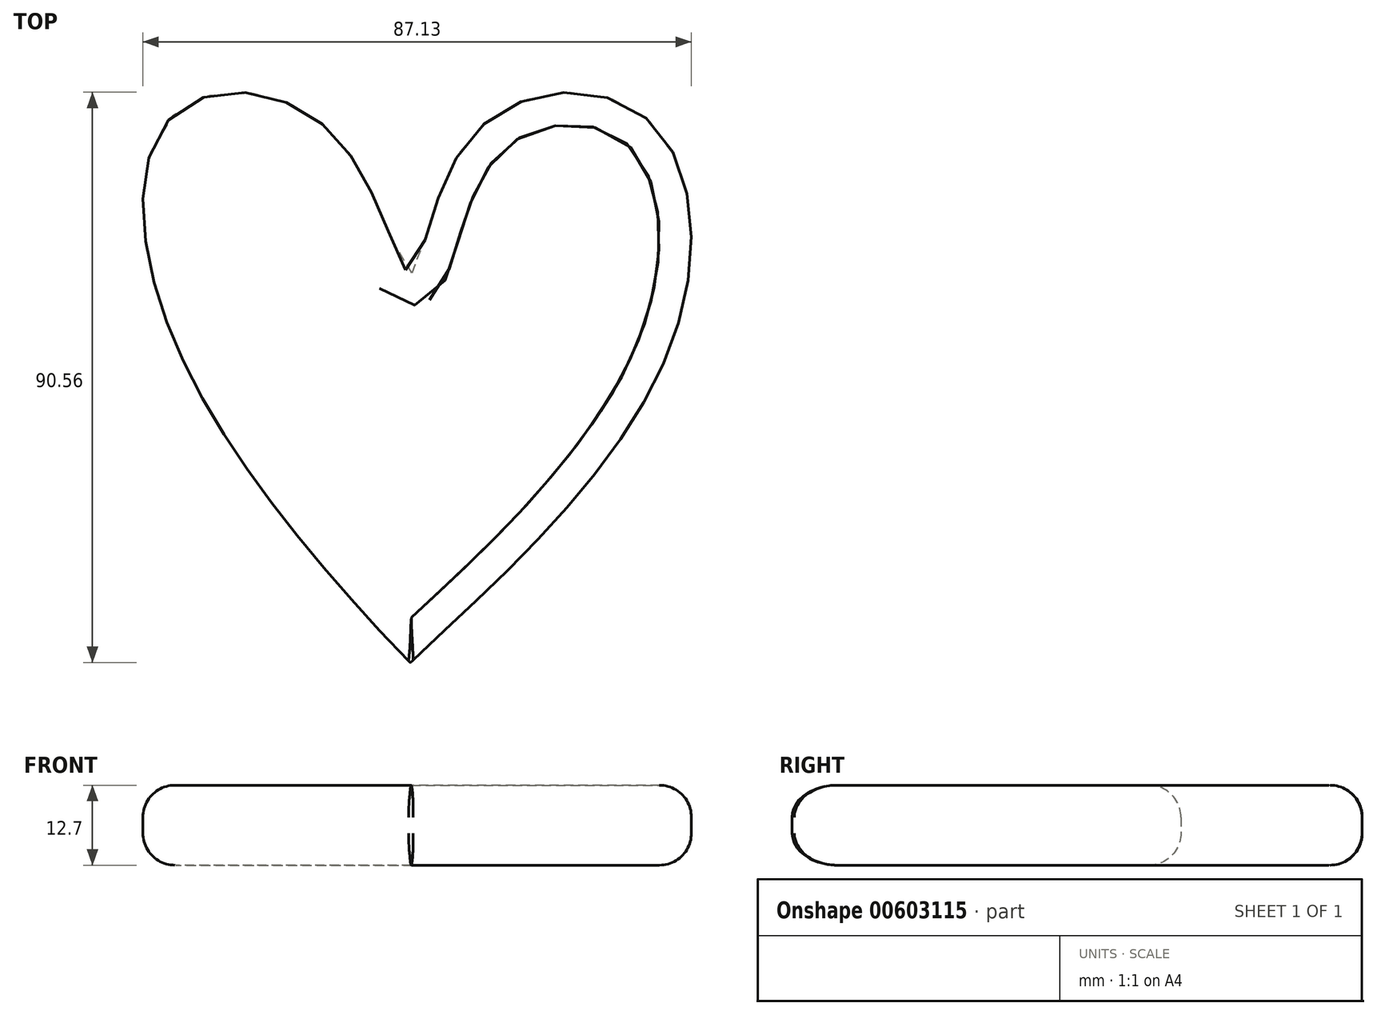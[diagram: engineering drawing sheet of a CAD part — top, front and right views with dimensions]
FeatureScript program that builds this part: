
annotation { "Feature Type Name" : "Feature", "Feature Type Description" : "" }
export const myFeature = defineFeature(function(context is Context, id is Id, definition is map)
    precondition{}
    {
        {
            var Q0;
            Q0=qCreatedBy(makeId("Top.planeOp"),FACE);
            var sketch = newSketch(context, id + "F0", { "sketchPlane" : qUnion([Q0])});
            skFitSpline(sketch, "E0", {"points": [v(0, 0) * mm, v(-0.14, 0.09) * mm, v(-34.43, 44.52) * mm, v(-37.1, 87.44) * mm, v(-11.8, 83.44) * mm, v(0, 61.76) * mm, v(9.57, 83.36) * mm, v(36.94, 86.87) * mm, v(40.09, 47.18) * mm, v(3.83, 3.6) * mm, v(0, 0) * mm]});
            skSolve(sketch);
        }
        {
            var Q0;
            Q0=makeQuery(id+"F0.imprint","IMPRINT",FACE,{"disambiguationData":[TD([[makeQuery(id+"F0.imprint","IMPRINT",EDGE,{"derivedFrom":sQuery(id+"F0.wireOp",EDGE,"E0")}),-1.0]])]});
            extrude(context, id + "F1", {"entities" : qUnion([Q0]), "oppositeDirection" : true, "depth" : 12.7 * mm, "offsetDistance" : 25.4 * mm});
        }
        {
            var Q0;
            Q0=makeQuery(id+"F1.opExtrude","CAP_EDGE",EDGE,{"disambiguationData":[OSD([sQuery(id+"F0.wireOp",EDGE,"E0"),sQuery(id+"F0.wireOp",EDGE,"E0")])],"isStart":true});
            var Q1;
            Q1=makeQuery(id+"F1.opExtrude","CAP_EDGE",EDGE,{"disambiguationData":[OSD([sQuery(id+"F0.wireOp",EDGE,"E0"),sQuery(id+"F0.wireOp",EDGE,"E0")])],"isStart":false});
            fillet(context, id + "F2", {"entities" : qUnion([Q0, Q1]), "radius" : 5.08 * mm, "tangentPropagation" : true, "allowEdgeOverflow" : false});
        }
    });
